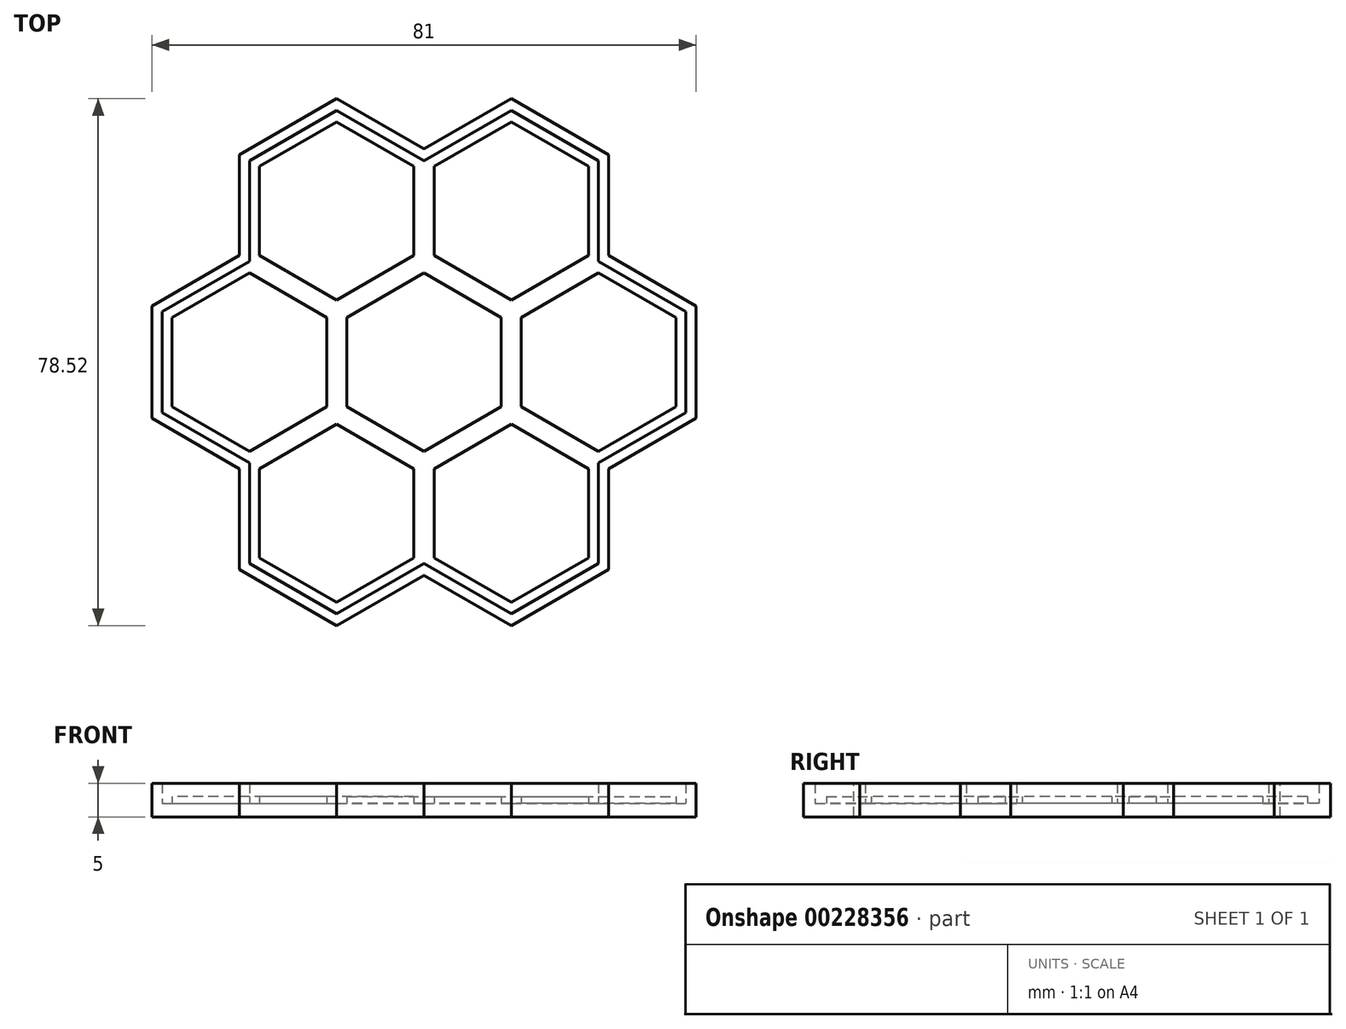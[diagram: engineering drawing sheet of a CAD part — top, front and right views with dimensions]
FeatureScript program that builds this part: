
annotation { "Feature Type Name" : "Feature", "Feature Type Description" : "" }
export const myFeature = defineFeature(function(context is Context, id is Id, definition is map)
    precondition{}
    {
        {
            var Q0;
            Q0=qCreatedBy(makeId("Top.planeOp"),FACE);
            var sketch = newSketch(context, id + "F0", { "sketchPlane" : qUnion([Q0])});
            skCircle(sketch, "E0.cCircle", {"center": v(0, 0) * mm, "radius": 11.5 * mm, "construction": true});
            skLineSegment(sketch, "E0.0", {"start": v(11.5, 6.64) * mm, "end": v(11.5, -6.64) * mm});
            skLineSegment(sketch, "E0.1", {"start": v(11.5, -6.64) * mm, "end": v(0, -13.28) * mm});
            skLineSegment(sketch, "E0.2", {"start": v(0, -13.28) * mm, "end": v(-11.5, -6.64) * mm});
            skLineSegment(sketch, "E0.3", {"start": v(-11.5, -6.64) * mm, "end": v(-11.5, 6.64) * mm});
            skLineSegment(sketch, "E0.4", {"start": v(-11.5, 6.64) * mm, "end": v(0, 13.28) * mm});
            skLineSegment(sketch, "E0.5", {"start": v(0, 13.28) * mm, "end": v(11.5, 6.64) * mm});
            skPoint(sketch, "E0.0.midPoint", {"position": v(11.5, 0) * mm});
            skCircle(sketch, "E1.cCircle", {"center": v(13, 22.52) * mm, "radius": 11.5 * mm, "construction": true});
            skLineSegment(sketch, "E1.0", {"start": v(24.5, 29.16) * mm, "end": v(24.5, 15.88) * mm});
            skLineSegment(sketch, "E1.1", {"start": v(24.5, 15.88) * mm, "end": v(13, 9.24) * mm});
            skLineSegment(sketch, "E1.2", {"start": v(13, 9.24) * mm, "end": v(1.5, 15.88) * mm});
            skLineSegment(sketch, "E1.3", {"start": v(1.5, 15.88) * mm, "end": v(1.5, 29.16) * mm});
            skLineSegment(sketch, "E1.4", {"start": v(1.5, 29.16) * mm, "end": v(13, 35.8) * mm});
            skLineSegment(sketch, "E1.5", {"start": v(13, 35.8) * mm, "end": v(24.5, 29.16) * mm});
            skPoint(sketch, "E1.0.midPoint", {"position": v(24.5, 22.52) * mm});
            skCircle(sketch, "E2.cCircle", {"center": v(26, 0) * mm, "radius": 11.5 * mm, "construction": true});
            skLineSegment(sketch, "E2.0", {"start": v(37.5, 6.64) * mm, "end": v(37.5, -6.64) * mm});
            skLineSegment(sketch, "E2.1", {"start": v(37.5, -6.64) * mm, "end": v(26, -13.28) * mm});
            skLineSegment(sketch, "E2.2", {"start": v(26, -13.28) * mm, "end": v(14.5, -6.64) * mm});
            skLineSegment(sketch, "E2.3", {"start": v(14.5, -6.64) * mm, "end": v(14.5, 6.64) * mm});
            skLineSegment(sketch, "E2.4", {"start": v(14.5, 6.64) * mm, "end": v(26, 13.28) * mm});
            skLineSegment(sketch, "E2.5", {"start": v(26, 13.28) * mm, "end": v(37.5, 6.64) * mm});
            skPoint(sketch, "E2.0.midPoint", {"position": v(37.5, 0) * mm});
            skCircle(sketch, "E3.cCircle", {"center": v(13, -22.52) * mm, "radius": 11.5 * mm, "construction": true});
            skLineSegment(sketch, "E3.0", {"start": v(24.5, -15.88) * mm, "end": v(24.5, -29.16) * mm});
            skLineSegment(sketch, "E3.1", {"start": v(24.5, -29.16) * mm, "end": v(13, -35.8) * mm});
            skLineSegment(sketch, "E3.2", {"start": v(13, -35.8) * mm, "end": v(1.5, -29.16) * mm});
            skLineSegment(sketch, "E3.3", {"start": v(1.5, -29.16) * mm, "end": v(1.5, -15.88) * mm});
            skLineSegment(sketch, "E3.4", {"start": v(1.5, -15.88) * mm, "end": v(13, -9.24) * mm});
            skLineSegment(sketch, "E3.5", {"start": v(13, -9.24) * mm, "end": v(24.5, -15.88) * mm});
            skPoint(sketch, "E3.0.midPoint", {"position": v(24.5, -22.52) * mm});
            skCircle(sketch, "E4.cCircle", {"center": v(-13, -22.52) * mm, "radius": 11.5 * mm, "construction": true});
            skLineSegment(sketch, "E4.0", {"start": v(-24.5, -29.16) * mm, "end": v(-24.5, -15.88) * mm});
            skLineSegment(sketch, "E4.1", {"start": v(-24.5, -15.88) * mm, "end": v(-13, -9.24) * mm});
            skLineSegment(sketch, "E4.2", {"start": v(-13, -9.24) * mm, "end": v(-1.5, -15.88) * mm});
            skLineSegment(sketch, "E4.3", {"start": v(-1.5, -15.88) * mm, "end": v(-1.5, -29.16) * mm});
            skLineSegment(sketch, "E4.4", {"start": v(-1.5, -29.16) * mm, "end": v(-13, -35.8) * mm});
            skLineSegment(sketch, "E4.5", {"start": v(-13, -35.8) * mm, "end": v(-24.5, -29.16) * mm});
            skPoint(sketch, "E4.0.midPoint", {"position": v(-24.5, -22.52) * mm});
            skCircle(sketch, "E5.cCircle", {"center": v(-26, 0) * mm, "radius": 11.5 * mm, "construction": true});
            skLineSegment(sketch, "E5.0", {"start": v(-37.5, -6.64) * mm, "end": v(-37.5, 6.64) * mm});
            skLineSegment(sketch, "E5.1", {"start": v(-37.5, 6.64) * mm, "end": v(-26, 13.28) * mm});
            skLineSegment(sketch, "E5.2", {"start": v(-26, 13.28) * mm, "end": v(-14.5, 6.64) * mm});
            skLineSegment(sketch, "E5.3", {"start": v(-14.5, 6.64) * mm, "end": v(-14.5, -6.64) * mm});
            skLineSegment(sketch, "E5.4", {"start": v(-14.5, -6.64) * mm, "end": v(-26, -13.28) * mm});
            skLineSegment(sketch, "E5.5", {"start": v(-26, -13.28) * mm, "end": v(-37.5, -6.64) * mm});
            skPoint(sketch, "E5.0.midPoint", {"position": v(-37.5, 0) * mm});
            skCircle(sketch, "E6.cCircle", {"center": v(-13, 22.52) * mm, "radius": 11.5 * mm, "construction": true});
            skLineSegment(sketch, "E6.0", {"start": v(-1.5, 29.16) * mm, "end": v(-1.5, 15.88) * mm});
            skLineSegment(sketch, "E6.1", {"start": v(-1.5, 15.88) * mm, "end": v(-13, 9.24) * mm});
            skLineSegment(sketch, "E6.2", {"start": v(-13, 9.24) * mm, "end": v(-24.5, 15.88) * mm});
            skLineSegment(sketch, "E6.3", {"start": v(-24.5, 15.88) * mm, "end": v(-24.5, 29.16) * mm});
            skLineSegment(sketch, "E6.4", {"start": v(-24.5, 29.16) * mm, "end": v(-13, 35.8) * mm});
            skLineSegment(sketch, "E6.5", {"start": v(-13, 35.8) * mm, "end": v(-1.5, 29.16) * mm});
            skPoint(sketch, "E6.0.midPoint", {"position": v(-1.5, 22.52) * mm});
            skLineSegment(sketch, "E7", {"start": v(-26, 0) * mm, "end": v(26, 0) * mm, "construction": true});
            skLineSegment(sketch, "E8", {"start": v(13, -22.52) * mm, "end": v(-13, 22.52) * mm, "construction": true});
            skLineSegment(sketch, "E9", {"start": v(-13, -22.52) * mm, "end": v(13, 22.52) * mm, "construction": true});
            skLineSegment(sketch, "E10.0", {"start": v(-39, 7.5) * mm, "end": v(-26, 15.01) * mm});
            skLineSegment(sketch, "E10.1", {"start": v(-39, -7.5) * mm, "end": v(-39, 7.5) * mm});
            skLineSegment(sketch, "E10.2", {"start": v(-26, -15.01) * mm, "end": v(-39, -7.5) * mm});
            skLineSegment(sketch, "E11.0", {"start": v(-13, 37.53) * mm, "end": v(0, 30.02) * mm});
            skLineSegment(sketch, "E11.1", {"start": v(-26, 30.02) * mm, "end": v(-13, 37.53) * mm});
            skLineSegment(sketch, "E11.2", {"start": v(-26, 15.01) * mm, "end": v(-26, 30.02) * mm});
            skLineSegment(sketch, "E12.0", {"start": v(26, 30.02) * mm, "end": v(26, 15.01) * mm});
            skLineSegment(sketch, "E12.1", {"start": v(13, 37.53) * mm, "end": v(26, 30.02) * mm});
            skLineSegment(sketch, "E12.2", {"start": v(0, 30.02) * mm, "end": v(13, 37.53) * mm});
            skLineSegment(sketch, "E13.0", {"start": v(39, -7.5) * mm, "end": v(26, -15.01) * mm});
            skLineSegment(sketch, "E13.1", {"start": v(39, 7.5) * mm, "end": v(39, -7.5) * mm});
            skLineSegment(sketch, "E13.2", {"start": v(26, 15.01) * mm, "end": v(39, 7.5) * mm});
            skLineSegment(sketch, "E14.0", {"start": v(13, -37.53) * mm, "end": v(0, -30.02) * mm});
            skLineSegment(sketch, "E14.1", {"start": v(26, -30.02) * mm, "end": v(13, -37.53) * mm});
            skLineSegment(sketch, "E14.2", {"start": v(26, -15.01) * mm, "end": v(26, -30.02) * mm});
            skLineSegment(sketch, "E15.0", {"start": v(-26, -30.02) * mm, "end": v(-26, -15.01) * mm});
            skLineSegment(sketch, "E15.1", {"start": v(-13, -37.53) * mm, "end": v(-26, -30.02) * mm});
            skLineSegment(sketch, "E15.2", {"start": v(0, -30.02) * mm, "end": v(-13, -37.53) * mm});
            skLineSegment(sketch, "E16.0", {"start": v(-27.5, -15.88) * mm, "end": v(-40.5, -8.37) * mm});
            skLineSegment(sketch, "E16.1", {"start": v(-27.5, -30.89) * mm, "end": v(-27.5, -15.88) * mm});
            skLineSegment(sketch, "E16.2", {"start": v(-13, -39.26) * mm, "end": v(-27.5, -30.89) * mm});
            skLineSegment(sketch, "E16.3", {"start": v(0, -31.75) * mm, "end": v(-13, -39.26) * mm});
            skLineSegment(sketch, "E16.4", {"start": v(13, -39.26) * mm, "end": v(0, -31.75) * mm});
            skLineSegment(sketch, "E16.5", {"start": v(-40.5, -8.37) * mm, "end": v(-40.5, 8.37) * mm});
            skLineSegment(sketch, "E16.6", {"start": v(27.5, -30.89) * mm, "end": v(13, -39.26) * mm});
            skLineSegment(sketch, "E16.7", {"start": v(27.5, -15.88) * mm, "end": v(27.5, -30.89) * mm});
            skLineSegment(sketch, "E16.8", {"start": v(-13, 39.26) * mm, "end": v(0, 31.75) * mm});
            skLineSegment(sketch, "E16.9", {"start": v(-27.5, 30.89) * mm, "end": v(-13, 39.26) * mm});
            skLineSegment(sketch, "E16.10", {"start": v(-27.5, 15.88) * mm, "end": v(-27.5, 30.89) * mm});
            skLineSegment(sketch, "E16.11", {"start": v(-40.5, 8.37) * mm, "end": v(-27.5, 15.88) * mm});
            skLineSegment(sketch, "E16.12", {"start": v(0, 31.75) * mm, "end": v(13, 39.26) * mm});
            skLineSegment(sketch, "E16.13", {"start": v(13, 39.26) * mm, "end": v(27.5, 30.89) * mm});
            skLineSegment(sketch, "E16.14", {"start": v(27.5, 30.89) * mm, "end": v(27.5, 15.88) * mm});
            skLineSegment(sketch, "E16.15", {"start": v(27.5, 15.88) * mm, "end": v(40.5, 8.37) * mm});
            skLineSegment(sketch, "E16.16", {"start": v(40.5, 8.37) * mm, "end": v(40.5, -8.37) * mm});
            skLineSegment(sketch, "E16.17", {"start": v(40.5, -8.37) * mm, "end": v(27.5, -15.88) * mm});
            skSolve(sketch);
        }
        {
            var Q0;
            Q0 = qSketchRegion(id + "F0", true);
            var Q1;
            Q1=makeQuery(id+"F0.imprint","IMPRINT",FACE,{"disambiguationData":[TD([[makeQuery(id+"F0.imprint","IMPRINT",EDGE,{"derivedFrom":sQuery(id+"F0.wireOp",EDGE,"E0.0")}),1.0]])]});
            var Q2;
            Q2=makeQuery(id+"F0.imprint","IMPRINT",FACE,{"disambiguationData":[TD([[makeQuery(id+"F0.imprint","IMPRINT",EDGE,{"derivedFrom":sQuery(id+"F0.wireOp",EDGE,"E5.0")}),-1.0]])]});
            var Q3;
            Q3=makeQuery(id+"F0.imprint","IMPRINT",FACE,{"disambiguationData":[TD([[makeQuery(id+"F0.imprint","IMPRINT",EDGE,{"derivedFrom":sQuery(id+"F0.wireOp",EDGE,"E6.0")}),-1.0]])]});
            var Q4;
            Q4=makeQuery(id+"F0.imprint","IMPRINT",FACE,{"disambiguationData":[TD([[makeQuery(id+"F0.imprint","IMPRINT",EDGE,{"derivedFrom":sQuery(id+"F0.wireOp",EDGE,"E1.0")}),-1.0]])]});
            var Q5;
            Q5=makeQuery(id+"F0.imprint","IMPRINT",FACE,{"disambiguationData":[TD([[makeQuery(id+"F0.imprint","IMPRINT",EDGE,{"derivedFrom":sQuery(id+"F0.wireOp",EDGE,"E3.0")}),-1.0]])]});
            var Q6;
            Q6=makeQuery(id+"F0.imprint","IMPRINT",FACE,{"disambiguationData":[TD([[makeQuery(id+"F0.imprint","IMPRINT",EDGE,{"derivedFrom":sQuery(id+"F0.wireOp",EDGE,"E4.0")}),-1.0]])]});
            var Q7;
            Q7=makeQuery(id+"F0.imprint","IMPRINT",FACE,{"disambiguationData":[TD([[makeQuery(id+"F0.imprint","IMPRINT",EDGE,{"derivedFrom":sQuery(id+"F0.wireOp",EDGE,"E0.0")}),-1.0]])]});
            var Q8;
            Q8=makeQuery(id+"F0.imprint","IMPRINT",FACE,{"disambiguationData":[TD([[makeQuery(id+"F0.imprint","IMPRINT",EDGE,{"derivedFrom":sQuery(id+"F0.wireOp",EDGE,"E2.0")}),-1.0]])]});
            extrude(context, id + "F1", {"entities" : qUnion([Q0, Q1, Q2, Q3, Q4, Q5, Q6, Q7, Q8]), "oppositeDirection" : true, "depth" : 2 * mm});
        }
        {
            var Q0;
            Q0=makeQuery(id+"F0.imprint","IMPRINT",FACE,{"disambiguationData":[TD([[makeQuery(id+"F0.imprint","IMPRINT",EDGE,{"derivedFrom":sQuery(id+"F0.wireOp",EDGE,"E5.0")}),-1.0]])]});
            var Q1;
            Q1=makeQuery(id+"F0.imprint","IMPRINT",FACE,{"disambiguationData":[TD([[makeQuery(id+"F0.imprint","IMPRINT",EDGE,{"derivedFrom":sQuery(id+"F0.wireOp",EDGE,"E6.0")}),-1.0]])]});
            var Q2;
            Q2=makeQuery(id+"F0.imprint","IMPRINT",FACE,{"disambiguationData":[TD([[makeQuery(id+"F0.imprint","IMPRINT",EDGE,{"derivedFrom":sQuery(id+"F0.wireOp",EDGE,"E1.0")}),-1.0]])]});
            var Q3;
            Q3=makeQuery(id+"F0.imprint","IMPRINT",FACE,{"disambiguationData":[TD([[makeQuery(id+"F0.imprint","IMPRINT",EDGE,{"derivedFrom":sQuery(id+"F0.wireOp",EDGE,"E2.0")}),-1.0]])]});
            var Q4;
            Q4=makeQuery(id+"F0.imprint","IMPRINT",FACE,{"disambiguationData":[TD([[makeQuery(id+"F0.imprint","IMPRINT",EDGE,{"derivedFrom":sQuery(id+"F0.wireOp",EDGE,"E3.0")}),-1.0]])]});
            var Q5;
            Q5=makeQuery(id+"F0.imprint","IMPRINT",FACE,{"disambiguationData":[TD([[makeQuery(id+"F0.imprint","IMPRINT",EDGE,{"derivedFrom":sQuery(id+"F0.wireOp",EDGE,"E4.0")}),-1.0]])]});
            var Q6;
            Q6=makeQuery(id+"F0.imprint","IMPRINT",FACE,{"disambiguationData":[TD([[makeQuery(id+"F0.imprint","IMPRINT",EDGE,{"derivedFrom":sQuery(id+"F0.wireOp",EDGE,"E0.0")}),-1.0]])]});
            extrude(context, id + "F2", {"entities" : qUnion([Q0, Q1, Q2, Q3, Q4, Q5, Q6]), "operationType" : NewBodyOperationType.ADD, "depth" : 1 * mm});
        }
        {
            var Q0;
            Q0=makeQuery(id+"F0.imprint","IMPRINT",FACE,{"disambiguationData":[TD([[makeQuery(id+"F0.imprint","IMPRINT",EDGE,{"derivedFrom":sQuery(id+"F0.wireOp",EDGE,"E10.0")}),1.0]])]});
            extrude(context, id + "F3", {"entities" : qUnion([Q0]), "operationType" : NewBodyOperationType.ADD, "depth" : 3 * mm});
        }
    });
